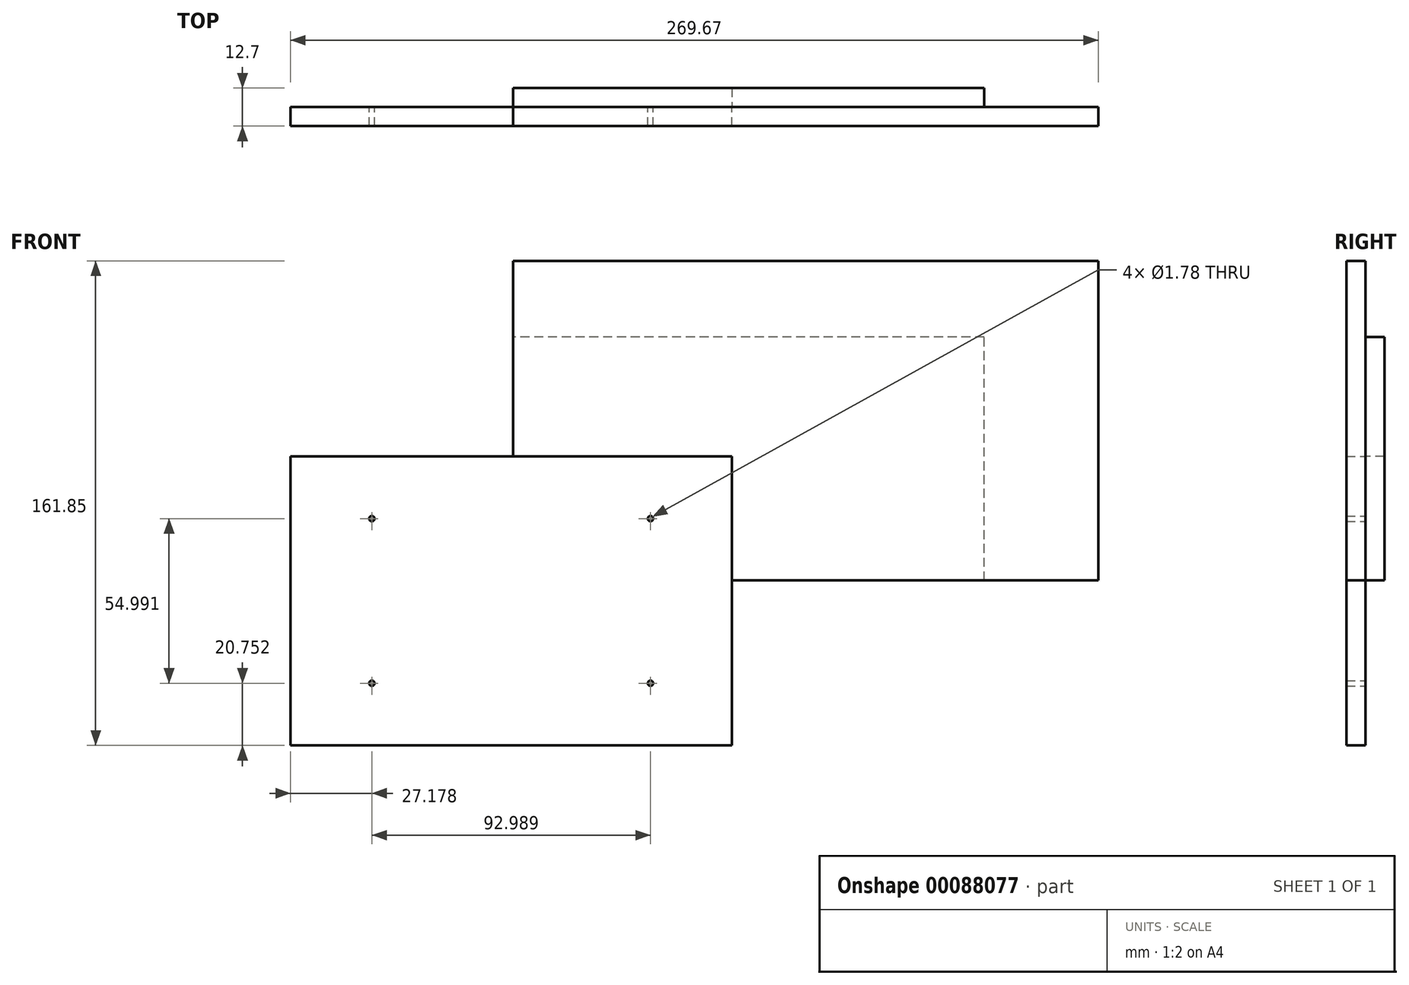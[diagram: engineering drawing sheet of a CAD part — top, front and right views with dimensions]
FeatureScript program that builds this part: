
annotation { "Feature Type Name" : "Feature", "Feature Type Description" : "" }
export const myFeature = defineFeature(function(context is Context, id is Id, definition is map)
    precondition{}
    {
        {
            var Q0;
            Q0=qCreatedBy(makeId("Front.planeOp"),FACE);
            var sketch = newSketch(context, id + "F0", { "sketchPlane" : qUnion([Q0])});
            skLineSegment(sketch, "E0", {"start": v(0, 0) * mm, "end": v(0, 48.26) * mm});
            skLineSegment(sketch, "E1", {"start": v(0, 96.52) * mm, "end": v(147.32, 96.52) * mm});
            skLineSegment(sketch, "E2", {"start": v(147.32, 96.52) * mm, "end": v(147.32, 0) * mm});
            skLineSegment(sketch, "E3", {"start": v(147.32, 0) * mm, "end": v(0, 0) * mm});
            skCircle(sketch, "E4", {"center": v(27.18, 20.75) * mm, "radius": 0.89 * mm});
            skCircle(sketch, "E5", {"center": v(120.17, 20.75) * mm, "radius": 0.89 * mm});
            skCircle(sketch, "E6", {"center": v(120.17, 75.74) * mm, "radius": 0.89 * mm});
            skCircle(sketch, "E7", {"center": v(27.18, 75.74) * mm, "radius": 0.89 * mm});
            skLineSegment(sketch, "E8", {"start": v(0, 48.26) * mm, "end": v(0, 96.52) * mm});
            skSolve(sketch);
        }
        {
            var Q0;
            Q0=makeQuery(id+"F0.imprint","IMPRINT",FACE,{"disambiguationData":[TD([[makeQuery(id+"F0.imprint","IMPRINT",EDGE,{"derivedFrom":sQuery(id+"F0.wireOp",EDGE,"E0")}),-1.0]])]});
            extrude(context, id + "F1", {"entities" : qUnion([Q0]), "depth" : 6.35 * mm});
        }
        {
            var Q0;
            Q0=qCreatedBy(makeId("Front.planeOp"),FACE);
            var sketch = newSketch(context, id + "F2", { "sketchPlane" : qUnion([Q0])});
            skLineSegment(sketch, "E9", {"start": v(74.34, 96.52) * mm, "end": v(74.34, 136.45) * mm});
            skLineSegment(sketch, "E10", {"start": v(74.34, 161.85) * mm, "end": v(269.67, 161.85) * mm});
            skLineSegment(sketch, "E11", {"start": v(269.67, 161.85) * mm, "end": v(269.67, 55.1) * mm});
            skLineSegment(sketch, "E12", {"start": v(269.67, 55.1) * mm, "end": v(231.57, 55.1) * mm});
            skLineSegment(sketch, "E13", {"start": v(74.34, 96.52) * mm, "end": v(147.32, 96.52) * mm});
            skLineSegment(sketch, "E14", {"start": v(147.32, 96.52) * mm, "end": v(147.32, 55.1) * mm});
            skLineSegment(sketch, "E15", {"start": v(231.57, 55.1) * mm, "end": v(231.57, 136.45) * mm});
            skLineSegment(sketch, "E16", {"start": v(231.57, 136.45) * mm, "end": v(74.34, 136.45) * mm});
            skLineSegment(sketch, "E17", {"start": v(74.34, 136.45) * mm, "end": v(74.34, 161.85) * mm});
            skLineSegment(sketch, "E18", {"start": v(231.57, 55.1) * mm, "end": v(147.32, 55.1) * mm});
            skSolve(sketch);
        }
        {
            var Q0;
            Q0=makeQuery(id+"F2.imprint","IMPRINT",FACE,{"disambiguationData":[TD([[makeQuery(id+"F2.imprint","IMPRINT",EDGE,{"derivedFrom":sQuery(id+"F2.wireOp",EDGE,"E9")}),-1.0]])]});
            var Q1;
            Q1=makeQuery(id+"F2.imprint","IMPRINT",FACE,{"disambiguationData":[TD([[makeQuery(id+"F2.imprint","IMPRINT",EDGE,{"derivedFrom":sQuery(id+"F2.wireOp",EDGE,"E10")}),-1.0]])]});
            extrude(context, id + "F3", {"entities" : qUnion([Q0, Q1]), "depth" : 6.35 * mm});
        }
        {
            var Q0;
            Q0=makeQuery(id+"F2.imprint","IMPRINT",FACE,{"disambiguationData":[TD([[makeQuery(id+"F2.imprint","IMPRINT",EDGE,{"derivedFrom":sQuery(id+"F2.wireOp",EDGE,"E9")}),-1.0]])]});
            extrude(context, id + "F4", {"entities" : qUnion([Q0]), "oppositeDirection" : true, "depth" : 6.35 * mm});
        }
    });
